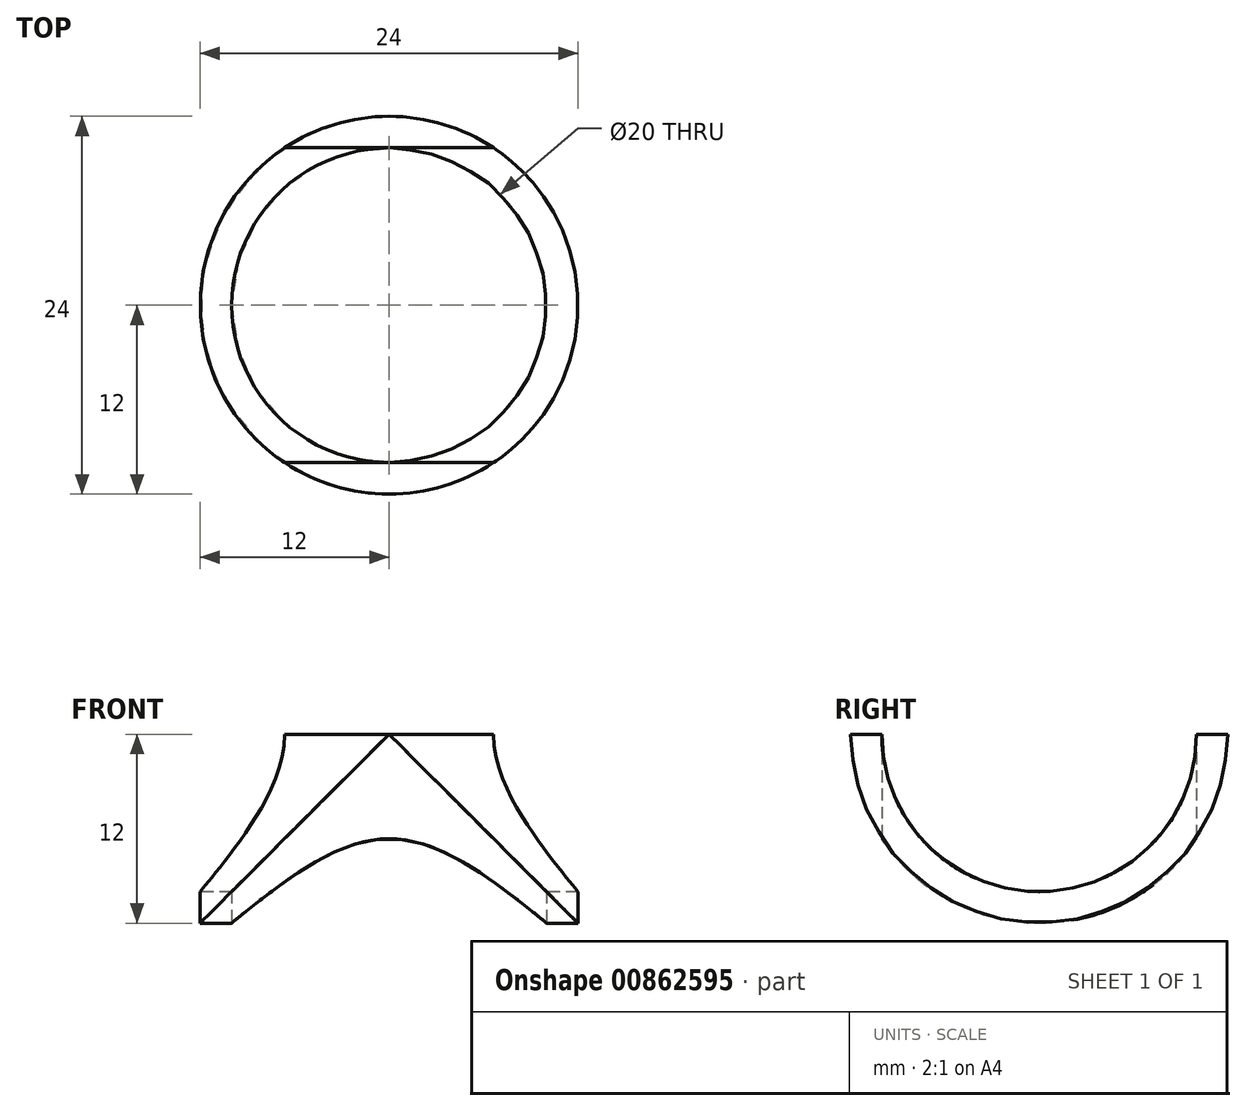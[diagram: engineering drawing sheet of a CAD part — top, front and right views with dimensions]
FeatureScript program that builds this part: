
annotation { "Feature Type Name" : "Feature", "Feature Type Description" : "" }
export const myFeature = defineFeature(function(context is Context, id is Id, definition is map)
    precondition{}
    {
        {
            var Q0;
            Q0=qCreatedBy(makeId("Front.planeOp"),FACE);
            var sketch = newSketch(context, id + "F0", { "sketchPlane" : qUnion([Q0])});
            skLineSegment(sketch, "E0", {"start": v(0, 0) * mm, "end": v(-10, 0) * mm});
            skLineSegment(sketch, "E1", {"start": v(-26, 0) * mm, "end": v(-36, 0) * mm});
            skLineSegment(sketch, "E2", {"start": v(-18, -1) * mm, "end": v(-18, -23) * mm});
            skLineSegment(sketch, "E3", {"start": v(-26, 0) * mm, "end": v(-10, 0) * mm});
            skSolve(sketch);
        }
        {
            var Q0;
            Q0=qCreatedBy(makeId("Right.planeOp"),FACE);
            var sketch = newSketch(context, id + "F1", { "sketchPlane" : qUnion([Q0])});
            skCircle(sketch, "E4", {"center": v(0, 0) * mm, "radius": 12 * mm});
            skCircle(sketch, "E5.0", {"center": v(0, 0) * mm, "radius": 10 * mm});
            skSolve(sketch);
        }
        {
            var Q0;
            Q0=makeQuery(id+"F1.imprint","IMPRINT",FACE,{"disambiguationData":[TD([[makeQuery(id+"F1.imprint","IMPRINT",EDGE,{"derivedFrom":sQuery(id+"F1.wireOp",EDGE,"E4")}),1.0]])]});
            var Q1;
            Q1=qSketchRegion(id+"F0",true);
            var Q2;
            Q2 = qSketchRegion(id + "F3", true);
            var Q3;
            Q3=sQuery(id+"F0.wireOp",EDGE,"E1");
            var Q4;
            Q4=sQuery(id+"F0.wireOp",EDGE,"E0");
            var Q5;
            Q5=sQuery(id+"F0.wireOp",EDGE,"E3");
            sweep(context, id + "F2", {"profiles" : qUnion([Q0, Q1, Q2]), "path" : qUnion([Q3, Q4, Q5])});
        }
        {
            var Q0;
            Q0=qCreatedBy(makeId("Top.planeOp"),FACE);
            var sketch = newSketch(context, id + "F3", { "sketchPlane" : qUnion([Q0])});
            skCircle(sketch, "E6", {"center": v(-18, 0) * mm, "radius": 12 * mm});
            skCircle(sketch, "E7.0", {"center": v(-18, 0) * mm, "radius": 10 * mm});
            skSolve(sketch);
        }
        {
            var Q0;
            Q0 = qSketchRegion(id + "F3", true);
            var Q1;
            Q1=sQuery(id+"F0.wireOp",EDGE,"E2");
            sweep(context, id + "F4", {"profiles" : qUnion([Q0]), "path" : qUnion([Q1])});
        }
        {
            var Q0;
            Q0=makeQuery(id+"F2.opSweep","SWEPT_BODY",BODY,{"disambiguationData":[OSD([sQuery(id+"F0.wireOp",EDGE,"E0"),sQuery(id+"F1.wireOp",EDGE,"E4"),sQuery(id+"F1.wireOp",EDGE,"E5.0")])]});
            var Q1;
            Q1=makeQuery(id+"F4.opSweep","SWEPT_BODY",BODY,{"disambiguationData":[OSD([sQuery(id+"F0.wireOp",EDGE,"E2"),sQuery(id+"F3.wireOp",EDGE,"E6"),sQuery(id+"F3.wireOp",EDGE,"E7.0")])]});
            booleanBodies(context, id + "F5", {"operationType" : BooleanOperationType.INTERSECTION, "tools" : qUnion([Q0, Q1]), "keepTools" : true});
        }
        {
            var Q0;
            Q0=makeQuery(id+"F5.opBoolean","INTERSECT",BODY,{"derivedFrom":[makeQuery(id+"F2.opSweep","SWEPT_BODY",BODY,{"disambiguationData":[OSD([sQuery(id+"F0.wireOp",EDGE,"E0"),sQuery(id+"F1.wireOp",EDGE,"E4"),sQuery(id+"F1.wireOp",EDGE,"E5.0")])]}),makeQuery(id+"F4.opSweep","SWEPT_BODY",BODY,{"disambiguationData":[OSD([sQuery(id+"F0.wireOp",EDGE,"E2"),sQuery(id+"F3.wireOp",EDGE,"E6"),sQuery(id+"F3.wireOp",EDGE,"E7.0")])]})]});
            var Q1;
            Q1=makeQuery(id+"F4.opSweep","SWEPT_BODY",BODY,{"disambiguationData":[OSD([sQuery(id+"F0.wireOp",EDGE,"E2"),sQuery(id+"F3.wireOp",EDGE,"E6"),sQuery(id+"F3.wireOp",EDGE,"E7.0")])]});
            booleanBodies(context, id + "F6", {"operationType" : BooleanOperationType.SUBTRACTION, "tools" : qUnion([Q0]), "targets" : qUnion([Q1]), "keepTools" : true});
        }
        {
            var Q0;
            Q0=makeQuery(id+"F5.opBoolean","INTERSECT",BODY,{"derivedFrom":[makeQuery(id+"F2.opSweep","SWEPT_BODY",BODY,{"disambiguationData":[OSD([sQuery(id+"F0.wireOp",EDGE,"E0"),sQuery(id+"F1.wireOp",EDGE,"E4"),sQuery(id+"F1.wireOp",EDGE,"E5.0")])]}),makeQuery(id+"F4.opSweep","SWEPT_BODY",BODY,{"disambiguationData":[OSD([sQuery(id+"F0.wireOp",EDGE,"E2"),sQuery(id+"F3.wireOp",EDGE,"E6"),sQuery(id+"F3.wireOp",EDGE,"E7.0")])]})]});
            var Q1;
            Q1=makeQuery(id+"F2.opSweep","SWEPT_BODY",BODY,{"disambiguationData":[OSD([sQuery(id+"F0.wireOp",EDGE,"E0"),sQuery(id+"F1.wireOp",EDGE,"E4"),sQuery(id+"F1.wireOp",EDGE,"E5.0")])]});
            booleanBodies(context, id + "F7", {"operationType" : BooleanOperationType.SUBTRACTION, "tools" : qUnion([Q0]), "targets" : qUnion([Q1]), "keepTools" : true});
        }
        {
            var Q0;
            Q0=makeQuery(id+"F7.opBoolean","SPLIT",BODY,{"disambiguationData":[OD(1.0)],"derivedFrom":makeQuery(id+"F2.opSweep","SWEPT_BODY",BODY,{"disambiguationData":[OSD([sQuery(id+"F0.wireOp",EDGE,"E0"),sQuery(id+"F1.wireOp",EDGE,"E4"),sQuery(id+"F1.wireOp",EDGE,"E5.0")])]})});
            var Q1;
            Q1=makeQuery(id+"F6.opBoolean","SPLIT",BODY,{"disambiguationData":[OD(1.0)],"derivedFrom":makeQuery(id+"F4.opSweep","SWEPT_BODY",BODY,{"disambiguationData":[OSD([sQuery(id+"F0.wireOp",EDGE,"E2"),sQuery(id+"F3.wireOp",EDGE,"E6"),sQuery(id+"F3.wireOp",EDGE,"E7.0")])]})});
            var Q2;
            Q2=makeQuery(id+"F6.opBoolean","SPLIT",BODY,{"disambiguationData":[OD(2.0)],"derivedFrom":makeQuery(id+"F4.opSweep","SWEPT_BODY",BODY,{"disambiguationData":[OSD([sQuery(id+"F0.wireOp",EDGE,"E2"),sQuery(id+"F3.wireOp",EDGE,"E6"),sQuery(id+"F3.wireOp",EDGE,"E7.0")])]})});
            deleteBodies(context, id + "F8", {"entities" : qUnion([Q0, Q1, Q2])});
        }
    });
